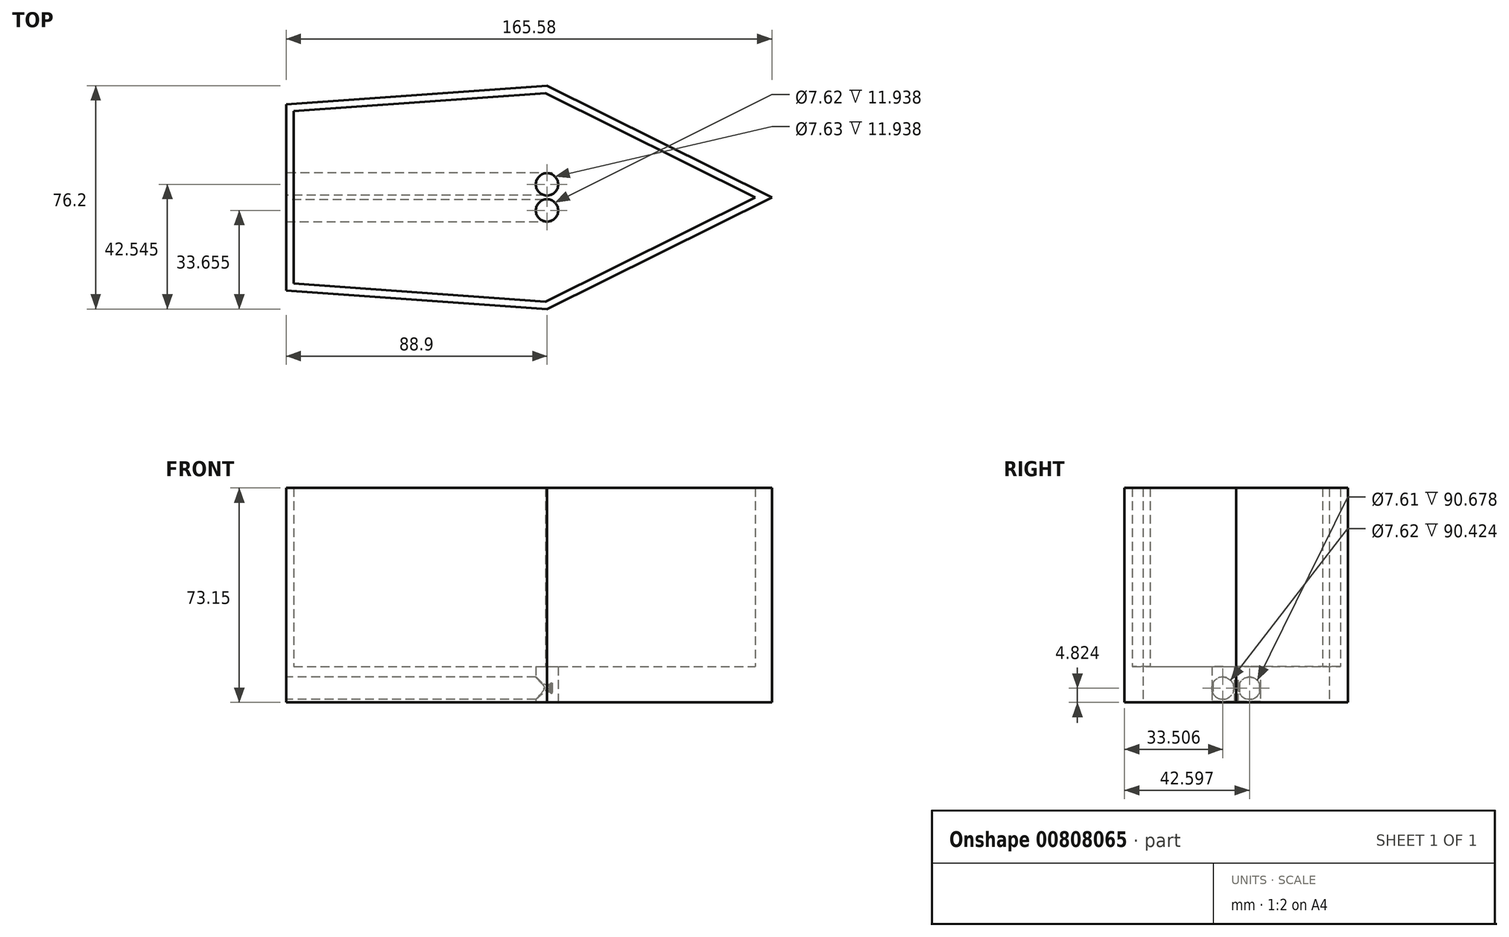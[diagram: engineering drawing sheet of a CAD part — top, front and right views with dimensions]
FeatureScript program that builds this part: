
annotation { "Feature Type Name" : "Feature", "Feature Type Description" : "" }
export const myFeature = defineFeature(function(context is Context, id is Id, definition is map)
    precondition{}
    {
        {
            var Q0;
            Q0=qCreatedBy(makeId("Top.planeOp"),FACE);
            var sketch = newSketch(context, id + "F0", { "sketchPlane" : qUnion([Q0])});
            skLineSegment(sketch, "E0", {"start": v(0, 38.1) * mm, "end": v(0, 0) * mm});
            skLineSegment(sketch, "E1", {"start": v(0, 0) * mm, "end": v(0, -38.1) * mm});
            skLineSegment(sketch, "E2", {"start": v(0, 0) * mm, "end": v(-88.9, 0) * mm});
            skLineSegment(sketch, "E3", {"start": v(0, 0) * mm, "end": v(50.8, 0) * mm});
            skLineSegment(sketch, "E4", {"start": v(-88.9, 0) * mm, "end": v(-88.9, -31.75) * mm});
            skLineSegment(sketch, "E5", {"start": v(-88.9, 0) * mm, "end": v(-88.9, 31.75) * mm});
            skLineSegment(sketch, "E6", {"start": v(-88.9, 31.75) * mm, "end": v(0, 38.1) * mm});
            skLineSegment(sketch, "E7", {"start": v(-88.9, -31.75) * mm, "end": v(0, -38.1) * mm});
            skLineSegment(sketch, "E8", {"start": v(0, 38.1) * mm, "end": v(76.68, 0) * mm});
            skLineSegment(sketch, "E9", {"start": v(0, -38.1) * mm, "end": v(76.68, 0) * mm});
            skSolve(sketch);
        }
        {
            var Q0;
            Q0 = qSketchRegion(id + "F0", true);
            extrude(context, id + "F1", {"entities" : qUnion([Q0]), "depth" : 63.5 * mm, "offsetDistance" : 25.4 * mm});
        }
        {
            var Q0;
            Q0=makeQuery(id+"F1.opExtrude","CAP_FACE",FACE,{"disambiguationData":[OSD([sQuery(id+"F0.wireOp",EDGE,"E4"),sQuery(id+"F0.wireOp",EDGE,"E5"),sQuery(id+"F0.wireOp",EDGE,"E6"),sQuery(id+"F0.wireOp",EDGE,"E7"),sQuery(id+"F0.wireOp",EDGE,"E8"),sQuery(id+"F0.wireOp",EDGE,"E9")])],"isStart":false});
            shell(context, id + "F2", {"entities" : qUnion([Q0]), "thickness" : 2.54 * mm});
        }
        {
            var Q0;
            Q0=makeQuery(id+"F1.opExtrude","CAP_FACE",FACE,{"disambiguationData":[OSD([sQuery(id+"F0.wireOp",EDGE,"E4"),sQuery(id+"F0.wireOp",EDGE,"E5"),sQuery(id+"F0.wireOp",EDGE,"E6"),sQuery(id+"F0.wireOp",EDGE,"E7"),sQuery(id+"F0.wireOp",EDGE,"E8"),sQuery(id+"F0.wireOp",EDGE,"E9")])],"isStart":true});
            var sketch = newSketch(context, id + "F3", { "sketchPlane" : qUnion([Q0])});
            skLineSegment(sketch, "E10", {"start": v(0, 0) * mm, "end": v(0, 4.45) * mm});
            skLineSegment(sketch, "E11", {"start": v(0, 0) * mm, "end": v(0, -4.45) * mm});
            skCircle(sketch, "E12", {"center": v(0, -4.45) * mm, "radius": 3.81 * mm});
            skCircle(sketch, "E13", {"center": v(0, 4.45) * mm, "radius": 3.81 * mm});
            skSolve(sketch);
        }
        {
            var Q0;
            Q0=makeQuery(id+"F3.imprint","IMPRINT",FACE,{"disambiguationData":[TD([[makeQuery(id+"F3.imprint","IMPRINT",EDGE,{"derivedFrom":sQuery(id+"F3.wireOp",EDGE,"E12")}),1.0]])]});
            var Q1;
            Q1=makeQuery(id+"F3.imprint","IMPRINT",FACE,{"disambiguationData":[TD([[makeQuery(id+"F3.imprint","IMPRINT",EDGE,{"derivedFrom":sQuery(id+"F3.wireOp",EDGE,"E13")}),1.0]])]});
            extrude(context, id + "F4", {"entities" : qUnion([Q0, Q1]), "operationType" : NewBodyOperationType.REMOVE, "oppositeDirection" : true, "depth" : 25.4 * mm, "offsetDistance" : 25.4 * mm});
        }
        {
            var Q0;
            Q0=makeQuery(id+"F1.opExtrude","CAP_FACE",FACE,{"disambiguationData":[OSD([sQuery(id+"F0.wireOp",EDGE,"E4"),sQuery(id+"F0.wireOp",EDGE,"E5"),sQuery(id+"F0.wireOp",EDGE,"E6"),sQuery(id+"F0.wireOp",EDGE,"E7"),sQuery(id+"F0.wireOp",EDGE,"E8"),sQuery(id+"F0.wireOp",EDGE,"E9")])],"isStart":true});
            extrude(context, id + "F5", {"entities" : qUnion([Q0]), "operationType" : NewBodyOperationType.ADD, "depth" : 9.65 * mm, "offsetDistance" : 25.4 * mm});
        }
        {
            var Q0;
            Q0=makeQuery(id+"F5.opExtrude","CAP_FACE",FACE,{"disambiguationData":[OSD([sQuery(id+"F0.wireOp",EDGE,"E4"),sQuery(id+"F0.wireOp",EDGE,"E5"),sQuery(id+"F0.wireOp",EDGE,"E6"),sQuery(id+"F0.wireOp",EDGE,"E7"),sQuery(id+"F0.wireOp",EDGE,"E8"),sQuery(id+"F0.wireOp",EDGE,"E9")])],"isStart":false});
            var sketch = newSketch(context, id + "F6", { "sketchPlane" : qUnion([Q0])});
            skLineSegment(sketch, "E14", {"start": v(0, 4.45) * mm, "end": v(-88.9, 4.45) * mm});
            skLineSegment(sketch, "E15", {"start": v(0, -4.45) * mm, "end": v(-88.9, -4.45) * mm});
            skSolve(sketch);
        }
        {
            var Q0;
            {var subQ0=sQuery(id+"F0.wireOp",EDGE,"E5");var subQ1=sQuery(id+"F0.wireOp",EDGE,"E4");Q0=makeQuery(id+"F5.boolean.opBoolean","MERGE",FACE,{"derivedFrom":[makeQuery(id+"F1.opExtrude","SWEPT_FACE",FACE,{"disambiguationData":[OSD([subQ1,subQ0])]}),makeQuery(id+"F5.opExtrude","SWEPT_FACE",FACE,{"disambiguationData":[OSD([subQ1,subQ0])]})]});}
            var sketch = newSketch(context, id + "F7", { "sketchPlane" : qUnion([Q0])});
            skCircle(sketch, "E16", {"center": v(4.6, -4.83) * mm, "radius": 3.81 * mm});
            skCircle(sketch, "E17", {"center": v(-4.5, -4.83) * mm, "radius": 3.8 * mm});
            skSolve(sketch);
        }
        {
            var Q0;
            Q0=makeQuery(id+"F7.imprint","IMPRINT",FACE,{"disambiguationData":[TD([[makeQuery(id+"F7.imprint","IMPRINT",EDGE,{"derivedFrom":sQuery(id+"F7.wireOp",EDGE,"E17")}),1.0]])]});
            extrude(context, id + "F8", {"entities" : qUnion([Q0]), "operationType" : NewBodyOperationType.REMOVE, "oppositeDirection" : true, "depth" : 90.68 * mm, "offsetDistance" : 25.4 * mm});
        }
        {
            var Q0;
            Q0=makeQuery(id+"F6.imprint","IMPRINT",FACE,{"disambiguationData":[TD([[makeQuery(id+"F6.imprint","IMPRINT",EDGE,{"derivedFrom":makeQuery(id+"F5.opExtrude","CAP_EDGE",EDGE,{"disambiguationData":[OSD([sQuery(id+"F3.wireOp",EDGE,"E12")])],"isStart":false})}),1.0]])]});
            extrude(context, id + "F9", {"entities" : qUnion([Q0]), "operationType" : NewBodyOperationType.ADD, "oppositeDirection" : true, "depth" : 0.25 * mm, "offsetDistance" : 25.4 * mm});
        }
        {
            var Q0;
            Q0=makeQuery(id+"F7.imprint","IMPRINT",FACE,{"disambiguationData":[TD([[makeQuery(id+"F7.imprint","IMPRINT",EDGE,{"derivedFrom":sQuery(id+"F7.wireOp",EDGE,"E16")}),1.0]])]});
            var Q1;
            Q1=sQuery(id+"F7.wireOp",EDGE,"E16");
            extrude(context, id + "F10", {"entities" : qUnion([Q0]), "operationType" : NewBodyOperationType.REMOVE, "surfaceEntities" : qUnion([Q1]), "oppositeDirection" : true, "depth" : 90.42 * mm, "offsetDistance" : 25.4 * mm});
        }
        {
            var Q0;
            Q0=makeQuery(id+"F9.boolean.opBoolean","MERGE",FACE,{"derivedFrom":[makeQuery(id+"F5.opExtrude","CAP_FACE",FACE,{"disambiguationData":[OSD([sQuery(id+"F0.wireOp",EDGE,"E4"),sQuery(id+"F0.wireOp",EDGE,"E5"),sQuery(id+"F0.wireOp",EDGE,"E6"),sQuery(id+"F0.wireOp",EDGE,"E7"),sQuery(id+"F0.wireOp",EDGE,"E8"),sQuery(id+"F0.wireOp",EDGE,"E9")])],"isStart":false}),makeQuery(id+"F9.opExtrude","CAP_FACE",FACE,{"disambiguationData":[OSD([sQuery(id+"F3.wireOp",EDGE,"E12")])],"isStart":true})]});
            var sketch = newSketch(context, id + "F11", { "sketchPlane" : qUnion([Q0])});
            skCircle(sketch, "E18", {"center": v(0, 4.45) * mm, "radius": 3.91 * mm});
            skSolve(sketch);
        }
        {
            var Q0;
            Q0 = qSketchRegion(id + "F11", true);
            extrude(context, id + "F12", {"entities" : qUnion([Q0]), "operationType" : NewBodyOperationType.ADD, "oppositeDirection" : true, "depth" : 0.25 * mm, "offsetDistance" : 25.4 * mm});
        }
    });
